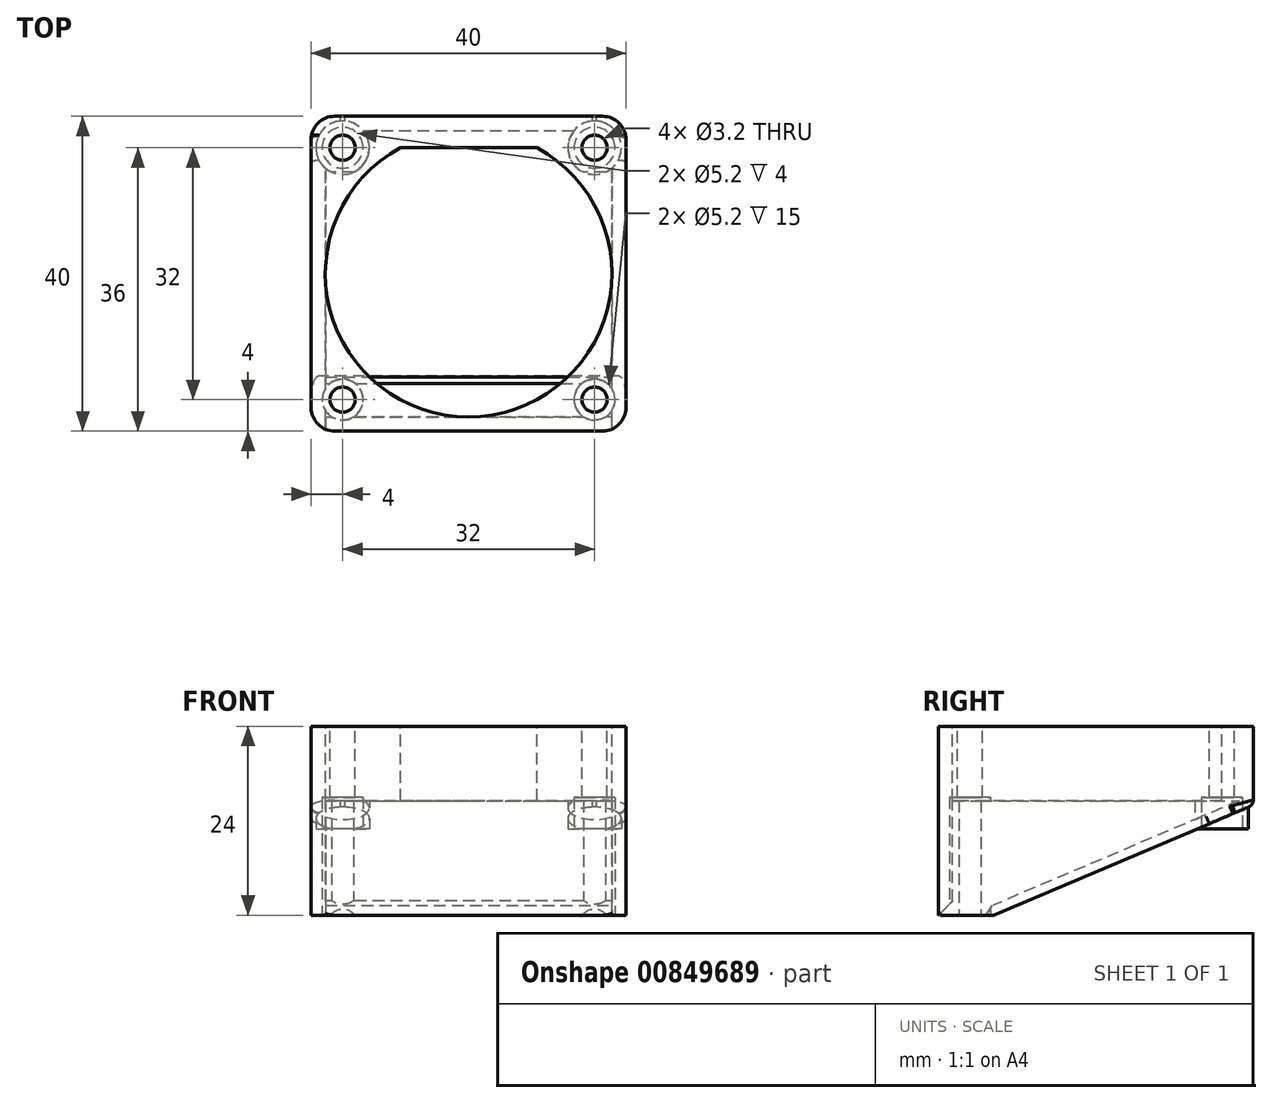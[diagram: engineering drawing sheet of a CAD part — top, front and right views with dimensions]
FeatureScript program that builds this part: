
annotation { "Feature Type Name" : "Feature", "Feature Type Description" : "" }
export const myFeature = defineFeature(function(context is Context, id is Id, definition is map)
    precondition{}
    {
        {
            var Q0;
            Q0=qCreatedBy(makeId("Right.planeOp"),FACE);
            var sketch = newSketch(context, id + "F0", { "sketchPlane" : qUnion([Q0])});
            skLineSegment(sketch, "E0", {"start": v(20, 24) * mm, "end": v(-20, 24) * mm});
            skLineSegment(sketch, "E1", {"start": v(-20, 24) * mm, "end": v(-20, 0) * mm});
            skLineSegment(sketch, "E2", {"start": v(-20, 0) * mm, "end": v(-13, 0) * mm});
            skLineSegment(sketch, "E3", {"start": v(-13, 0) * mm, "end": v(20, 14) * mm});
            skLineSegment(sketch, "E4", {"start": v(20, 14) * mm, "end": v(20, 24) * mm});
            skSolve(sketch);
        }
        {
            var Q0;
            Q0 = qSketchRegion(id + "F0", true);
            extrude(context, id + "F1", {"entities" : qUnion([Q0]), "endBound" : BoundingType.SYMMETRIC, "depth" : 40 * mm, "offsetDistance" : 25 * mm});
        }
        {
            var Q0;
            Q0=qCreatedBy(makeId("Right.planeOp"),FACE);
            cPlane(context, id + "F2", {"entities" : qUnion([Q0]), "cplaneType" : CPlaneType.OFFSET, "offset" : 18.2 * mm, "width" : 150 * mm, "height" : 150 * mm});
        }
        {
            var Q0;
            Q0=qCreatedBy(id+"F2.planeOp",FACE);
            var sketch = newSketch(context, id + "F3", { "sketchPlane" : qUnion([Q0])});
            skLineSegment(sketch, "E5", {"start": v(-18.2, 14.54) * mm, "end": v(18.2, 14.54) * mm});
            skLineSegment(sketch, "E6", {"start": v(18.2, 14.54) * mm, "end": v(-14.2, 0.8) * mm});
            skLineSegment(sketch, "E7", {"start": v(-14.2, 0.8) * mm, "end": v(-14.2, -5.89) * mm});
            skLineSegment(sketch, "E8", {"start": v(-14.2, -5.89) * mm, "end": v(-18.2, -5.89) * mm});
            skLineSegment(sketch, "E9", {"start": v(-18.2, -5.89) * mm, "end": v(-18.2, 14.54) * mm});
            skSolve(sketch);
        }
        {
            var Q0;
            Q0 = qSketchRegion(id + "F3", true);
            extrude(context, id + "F4", {"entities" : qUnion([Q0]), "operationType" : NewBodyOperationType.REMOVE, "oppositeDirection" : true, "depth" : 36.4 * mm, "offsetDistance" : 25 * mm});
        }
        {
            var Q0;
            Q0=makeQuery(id+"F1.opExtrude","SWEPT_FACE",FACE,{"disambiguationData":[OSD([sQuery(id+"F0.wireOp",EDGE,"E0")])]});
            var sketch = newSketch(context, id + "F5", { "sketchPlane" : qUnion([Q0])});
            skArc(sketch, "E10", {"start": v(-8.67, 16) * mm, "mid": v(0, -18.2) * mm, "end": v(8.67, 16) * mm});
            skLineSegment(sketch, "E11", {"start": v(-8.67, 16) * mm, "end": v(8.67, 16) * mm});
            skSolve(sketch);
        }
        {
            var Q0;
            Q0 = qSketchRegion(id + "F5", true);
            extrude(context, id + "F6", {"entities" : qUnion([Q0]), "operationType" : NewBodyOperationType.REMOVE, "oppositeDirection" : true, "depth" : 10 * mm, "offsetDistance" : 25 * mm});
        }
        {
            var Q0;
            Q0=makeQuery(id+"F1.opExtrude","SWEPT_FACE",FACE,{"disambiguationData":[OSD([sQuery(id+"F0.wireOp",EDGE,"E0")])]});
            var sketch = newSketch(context, id + "F7", { "sketchPlane" : qUnion([Q0])});
            skCircle(sketch, "E12", {"center": v(-16, 16) * mm, "radius": 1.6 * mm});
            skCircle(sketch, "E13", {"center": v(16, 16) * mm, "radius": 1.6 * mm});
            skCircle(sketch, "E14", {"center": v(-16, -16) * mm, "radius": 1.6 * mm});
            skCircle(sketch, "E15", {"center": v(16, -16) * mm, "radius": 1.6 * mm});
            skSolve(sketch);
        }
        {
            var Q0;
            Q0=makeQuery(id+"F4.boolean.opBoolean","INTERSECT",EDGE,{"derivedFrom":[makeQuery(id+"F1.opExtrude","SWEPT_FACE",FACE,{"disambiguationData":[OSD([sQuery(id+"F0.wireOp",EDGE,"E2")])]}),makeQuery(id+"F4.opExtrude","SWEPT_FACE",FACE,{"disambiguationData":[OSD([sQuery(id+"F3.wireOp",EDGE,"E9")])]})]});
            var Q1;
            Q1=makeQuery(id+"F4.boolean.opBoolean","COPY",EDGE,{"derivedFrom":makeQuery(id+"F4.opExtrude","SWEPT_EDGE",EDGE,{"disambiguationData":[OSD([sQuery(id+"F3.wireOp",EDGE,"E6"),sQuery(id+"F3.wireOp",EDGE,"E7")])]})});
            chamfer(context, id + "F8", {"entities" : qUnion([Q0, Q1]), "width" : 1.8 * mm, "tangentPropagation" : true});
        }
        {
            var Q0;
            Q0=qCreatedBy(makeId("Top.planeOp"),FACE);
            cPlane(context, id + "F9", {"entities" : qUnion([Q0]), "cplaneType" : CPlaneType.OFFSET, "offset" : 11 * mm, "width" : 150 * mm, "height" : 150 * mm});
        }
        {
            var Q0;
            Q0=qCreatedBy(id+"F9.planeOp",FACE);
            var sketch = newSketch(context, id + "F10", { "sketchPlane" : qUnion([Q0])});
            skCircle(sketch, "E16", {"center": v(-16, 16) * mm, "radius": 3.4 * mm});
            skCircle(sketch, "E17", {"center": v(16, 16) * mm, "radius": 3.4 * mm});
            skSolve(sketch);
        }
        {
            var Q0;
            Q0 = qSketchRegion(id + "F10", true);
            extrude(context, id + "F11", {"entities" : qUnion([Q0]), "operationType" : NewBodyOperationType.ADD, "depth" : 6 * mm, "offsetDistance" : 25 * mm});
        }
        {
            var Q0;
            Q0=qCreatedBy(makeId("Top.planeOp"),FACE);
            var sketch = newSketch(context, id + "F12", { "sketchPlane" : qUnion([Q0])});
            skCircle(sketch, "E18", {"center": v(-16, -16) * mm, "radius": 2.6 * mm});
            skCircle(sketch, "E19", {"center": v(16, -16) * mm, "radius": 2.6 * mm});
            skCircle(sketch, "E20", {"center": v(16, 16) * mm, "radius": 2.6 * mm});
            skCircle(sketch, "E21", {"center": v(-16, 16) * mm, "radius": 2.6 * mm});
            skSolve(sketch);
        }
        {
            var Q0;
            Q0 = qSketchRegion(id + "F12", true);
            extrude(context, id + "F13", {"entities" : qUnion([Q0]), "operationType" : NewBodyOperationType.REMOVE, "depth" : 15 * mm, "offsetDistance" : 25 * mm});
        }
        {
            var Q0;
            Q0 = qSketchRegion(id + "F7", true);
            extrude(context, id + "F14", {"entities" : qUnion([Q0]), "operationType" : NewBodyOperationType.REMOVE, "oppositeDirection" : true, "depth" : 25 * mm, "offsetDistance" : 25 * mm});
        }
        {
            var Q0;
            Q0=makeQuery(id+"F1.opExtrude","CAP_EDGE",EDGE,{"disambiguationData":[OSD([sQuery(id+"F0.wireOp",EDGE,"E1")])],"isStart":false});
            var Q1;
            Q1=makeQuery(id+"F1.opExtrude","CAP_EDGE",EDGE,{"disambiguationData":[OSD([sQuery(id+"F0.wireOp",EDGE,"E1")])],"isStart":true});
            var Q2;
            Q2=makeQuery(id+"F1.opExtrude","CAP_EDGE",EDGE,{"disambiguationData":[OSD([sQuery(id+"F0.wireOp",EDGE,"E4")])],"isStart":true});
            var Q3;
            Q3=makeQuery(id+"F1.opExtrude","CAP_EDGE",EDGE,{"disambiguationData":[OSD([sQuery(id+"F0.wireOp",EDGE,"E4")])],"isStart":false});
            fillet(context, id + "F15", {"entities" : qUnion([Q0, Q1, Q2, Q3]), "radius" : 3 * mm, "tangentPropagation" : true, "allowEdgeOverflow" : false});
        }
        {
            var Q0;
            Q0=makeQuery(id+"F1.opExtrude","SWEPT_EDGE",EDGE,{"disambiguationData":[OSD([sQuery(id+"F0.wireOp",EDGE,"E3"),sQuery(id+"F0.wireOp",EDGE,"E4")])]});
            var Q1;
            Q1=makeQuery(id+"F1.opExtrude","CAP_EDGE",EDGE,{"disambiguationData":[OSD([sQuery(id+"F0.wireOp",EDGE,"E3")])],"isStart":false});
            var Q2;
            Q2=makeQuery(id+"F1.opExtrude","CAP_EDGE",EDGE,{"disambiguationData":[OSD([sQuery(id+"F0.wireOp",EDGE,"E3")])],"isStart":true});
            var Q3;
            Q3=makeQuery(id+"F15.opFillet","BLEND_EDGE",EDGE,{"blendedFrom":[makeQuery(id+"F1.opExtrude","CAP_EDGE",EDGE,{"disambiguationData":[OSD([sQuery(id+"F0.wireOp",EDGE,"E4")])],"isStart":false}),makeQuery(id+"F1.opExtrude","SWEPT_FACE",FACE,{"disambiguationData":[OSD([sQuery(id+"F0.wireOp",EDGE,"E3")])]})],"blendedInto":[makeQuery(id+"F1.opExtrude","SWEPT_FACE",FACE,{"disambiguationData":[OSD([sQuery(id+"F0.wireOp",EDGE,"E3")])]})]});
            var Q4;
            Q4=makeQuery(id+"F15.opFillet","BLEND_EDGE",EDGE,{"blendedFrom":[makeQuery(id+"F1.opExtrude","CAP_EDGE",EDGE,{"disambiguationData":[OSD([sQuery(id+"F0.wireOp",EDGE,"E4")])],"isStart":true}),makeQuery(id+"F1.opExtrude","SWEPT_FACE",FACE,{"disambiguationData":[OSD([sQuery(id+"F0.wireOp",EDGE,"E3")])]})],"blendedInto":[makeQuery(id+"F1.opExtrude","SWEPT_FACE",FACE,{"disambiguationData":[OSD([sQuery(id+"F0.wireOp",EDGE,"E3")])]})]});
            fillet(context, id + "F16", {"entities" : qUnion([Q0, Q1, Q2, Q3, Q4]), "radius" : 1 * mm, "tangentPropagation" : true, "allowEdgeOverflow" : false});
        }
    });
